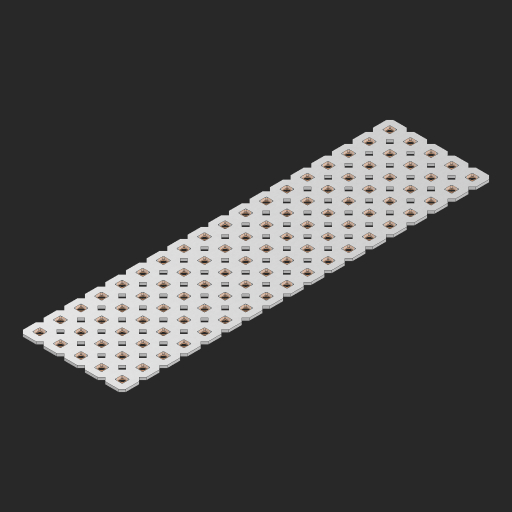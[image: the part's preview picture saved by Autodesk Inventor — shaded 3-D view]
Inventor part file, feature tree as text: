
AUTODESK INVENTOR PART (.ipt)
format: ipt  version: 2023 (Build 270158000, 158)  size: 1,323,520 bytes
history: native  units: in
note: dims shown in document units (in); Inventor stores cm internally (conversion verified against a paired STEP export)
features: other x91, extrude x89, sketch x2, pattern_linear x1
ambient origin geometry x8: Origin, YZ Plane, XZ Plane, XY Plane, X Axis, Y Axis, Z Axis, Center Point
bodies: Solid1 (feature_tree), Body (feature_tree)
feature tree (183):
  pattern_linear  "Rectangular Pattern1"  Spacing1=0.09in  [1 undecoded]
  sketch  "Sketch1"  dims[d1=0.5in]
  sketch  "Sketch2"  dims[d2=0.182in d3=0.09in d4=0.09in d5=0.09in d6=0.09in d7=0.09in d8=0.09in d9=0.09in d10=0.09in d11=0.02in d13=0.0in d14=0.172in d15=0.0625in d16=0.0in d19=0.5in d22=0.5in]
  other  "Srf1"
  other  "Srf126"
  other  "Srf127"
  other  "Srf128"
  other  "Srf129"
  other  "Srf130"
  other  "Srf131"
  other  "Srf250"
  other  "Srf251"
  other  "Srf252"
  other  "Srf253"
  other  "Srf254"
  other  "Srf255"
  other  "Srf256"
  other  "Srf257"
  other  "Srf258"
  other  "Srf259"
  other  "Srf260"
  other  "Srf268"
  other  "Srf269"
  other  "Srf270"
  other  "Srf271"
  other  "Srf272"
  other  "Srf273"
  other  "Srf274"
  other  "Srf275"
  other  "Srf276"
  other  "Srf277"
  other  "Srf278"
  other  "Srf279"
  other  "Srf280"
  other  "Srf281"
  other  "Srf282"
  other  "Srf283"
  other  "Srf284"
  other  "Srf285"
  other  "Srf293"
  other  "Srf294"
  other  "Srf295"
  other  "Srf296"
  other  "Srf297"
  other  "Srf298"
  other  "Srf299"
  other  "Srf300"
  other  "Srf301"
  other  "Srf302"
  other  "Srf303"
  other  "Srf304"
  other  "Srf305"
  other  "Srf306"
  other  "Srf307"
  other  "Srf308"
  other  "Srf309"
  other  "Srf310"
  other  "Srf318"
  other  "Srf319"
  other  "Srf320"
  other  "Srf321"
  other  "Srf322"
  other  "Srf323"
  other  "Srf324"
  other  "Srf325"
  other  "Srf326"
  other  "Srf327"
  other  "Srf328"
  other  "Srf329"
  other  "Srf330"
  other  "Srf331"
  other  "Srf332"
  other  "Srf333"
  other  "Srf334"
  other  "Srf335"
  other  "Srf343"
  other  "Srf344"
  other  "Srf345"
  other  "Srf346"
  other  "Srf347"
  other  "Srf348"
  other  "Srf349"
  other  "Srf350"
  other  "Srf351"
  other  "Srf352"
  other  "Srf353"
  other  "Srf354"
  other  "Srf355"
  other  "Srf356"
  other  "Srf357"
  other  "Srf358"
  other  "Srf359"
  other  "Srf360"
  other  "Circle"
  extrude  "ExtrusionSrf126"  Depth=0.09in
  extrude  "ExtrusionSrf127"  Depth=0.09in
  extrude  "ExtrusionSrf128"  Depth=0.09in
  extrude  "ExtrusionSrf129"  Depth=0.09in
  extrude  "ExtrusionSrf130"  Depth=0.09in
  extrude  "ExtrusionSrf131"  Depth=0.09in
  extrude  "ExtrusionSrf250"  Depth=0.09in
  extrude  "ExtrusionSrf251"  Depth=0.02in
  extrude  "ExtrusionSrf252"  TaperAngle=0.0deg  [1 undecoded]
  extrude  "ExtrusionSrf253"  Depth=0.5in
  extrude  "ExtrusionSrf254"  Depth=0.0625in TaperAngle=0.0deg
  extrude  "ExtrusionSrf255"  Depth=0.5in
  extrude  "ExtrusionSrf256"  Depth=0.5in
  extrude  "ExtrusionSrf257"  [1 undecoded]
  extrude  "ExtrusionSrf258"  [1 undecoded]
  extrude  "ExtrusionSrf259"  [1 undecoded]
  extrude  "ExtrusionSrf260"  [1 undecoded]
  extrude  "ExtrusionSrf268"  [1 undecoded]
  extrude  "ExtrusionSrf269"  [1 undecoded]
  extrude  "ExtrusionSrf270"  [1 undecoded]
  extrude  "ExtrusionSrf271"  [1 undecoded]
  extrude  "ExtrusionSrf272"  [1 undecoded]
  extrude  "ExtrusionSrf273"  [1 undecoded]
  extrude  "ExtrusionSrf274"  [1 undecoded]
  extrude  "ExtrusionSrf275"  [1 undecoded]
  extrude  "ExtrusionSrf276"  [1 undecoded]
  extrude  "ExtrusionSrf277"  [1 undecoded]
  extrude  "ExtrusionSrf278"  [1 undecoded]
  extrude  "ExtrusionSrf279"  [1 undecoded]
  extrude  "ExtrusionSrf280"  [1 undecoded]
  extrude  "ExtrusionSrf281"  [1 undecoded]
  extrude  "ExtrusionSrf282"  [1 undecoded]
  extrude  "ExtrusionSrf283"  [1 undecoded]
  extrude  "ExtrusionSrf284"  [1 undecoded]
  extrude  "ExtrusionSrf285"  [1 undecoded]
  extrude  "ExtrusionSrf293"  [1 undecoded]
  extrude  "ExtrusionSrf294"  [1 undecoded]
  extrude  "ExtrusionSrf295"  [1 undecoded]
  extrude  "ExtrusionSrf296"  [1 undecoded]
  extrude  "ExtrusionSrf297"  [1 undecoded]
  extrude  "ExtrusionSrf298"  [1 undecoded]
  extrude  "ExtrusionSrf299"  [1 undecoded]
  extrude  "ExtrusionSrf300"  [1 undecoded]
  extrude  "ExtrusionSrf301"  [1 undecoded]
  extrude  "ExtrusionSrf302"  [1 undecoded]
  extrude  "ExtrusionSrf303"  [1 undecoded]
  extrude  "ExtrusionSrf304"  [1 undecoded]
  extrude  "ExtrusionSrf305"  [1 undecoded]
  extrude  "ExtrusionSrf306"  [1 undecoded]
  extrude  "ExtrusionSrf307"  [1 undecoded]
  extrude  "ExtrusionSrf308"  [1 undecoded]
  extrude  "ExtrusionSrf309"  [1 undecoded]
  extrude  "ExtrusionSrf310"  [1 undecoded]
  extrude  "ExtrusionSrf318"  [1 undecoded]
  extrude  "ExtrusionSrf319"  [1 undecoded]
  extrude  "ExtrusionSrf320"  [1 undecoded]
  extrude  "ExtrusionSrf321"  [1 undecoded]
  extrude  "ExtrusionSrf322"  [1 undecoded]
  extrude  "ExtrusionSrf323"  [1 undecoded]
  extrude  "ExtrusionSrf324"  [1 undecoded]
  extrude  "ExtrusionSrf325"  [1 undecoded]
  extrude  "ExtrusionSrf326"  [1 undecoded]
  extrude  "ExtrusionSrf327"  [1 undecoded]
  extrude  "ExtrusionSrf328"  [1 undecoded]
  extrude  "ExtrusionSrf329"  [1 undecoded]
  extrude  "ExtrusionSrf330"  [1 undecoded]
  extrude  "ExtrusionSrf331"  [1 undecoded]
  extrude  "ExtrusionSrf332"  [1 undecoded]
  extrude  "ExtrusionSrf333"  [1 undecoded]
  extrude  "ExtrusionSrf334"  [1 undecoded]
  extrude  "ExtrusionSrf335"  [1 undecoded]
  extrude  "ExtrusionSrf343"  [1 undecoded]
  extrude  "ExtrusionSrf344"  [1 undecoded]
  extrude  "ExtrusionSrf345"  [1 undecoded]
  extrude  "ExtrusionSrf346"  [1 undecoded]
  extrude  "ExtrusionSrf347"  [1 undecoded]
  extrude  "ExtrusionSrf348"  [1 undecoded]
  extrude  "ExtrusionSrf349"  [1 undecoded]
  extrude  "ExtrusionSrf350"  [1 undecoded]
  extrude  "ExtrusionSrf351"  [1 undecoded]
  extrude  "ExtrusionSrf352"  [1 undecoded]
  extrude  "ExtrusionSrf353"  [1 undecoded]
  extrude  "ExtrusionSrf354"  [1 undecoded]
  extrude  "ExtrusionSrf355"  [1 undecoded]
  extrude  "ExtrusionSrf356"  [1 undecoded]
  extrude  "ExtrusionSrf357"  [1 undecoded]
  extrude  "ExtrusionSrf358"  [1 undecoded]
  extrude  "ExtrusionSrf359"  [1 undecoded]
  extrude  "ExtrusionSrf360"  [1 undecoded]
note: 78 required parameter values undecoded (feature->parameter linkage not recoverable at this tier; creation-order binding heuristic only, values carry confidence <= 0.55)
